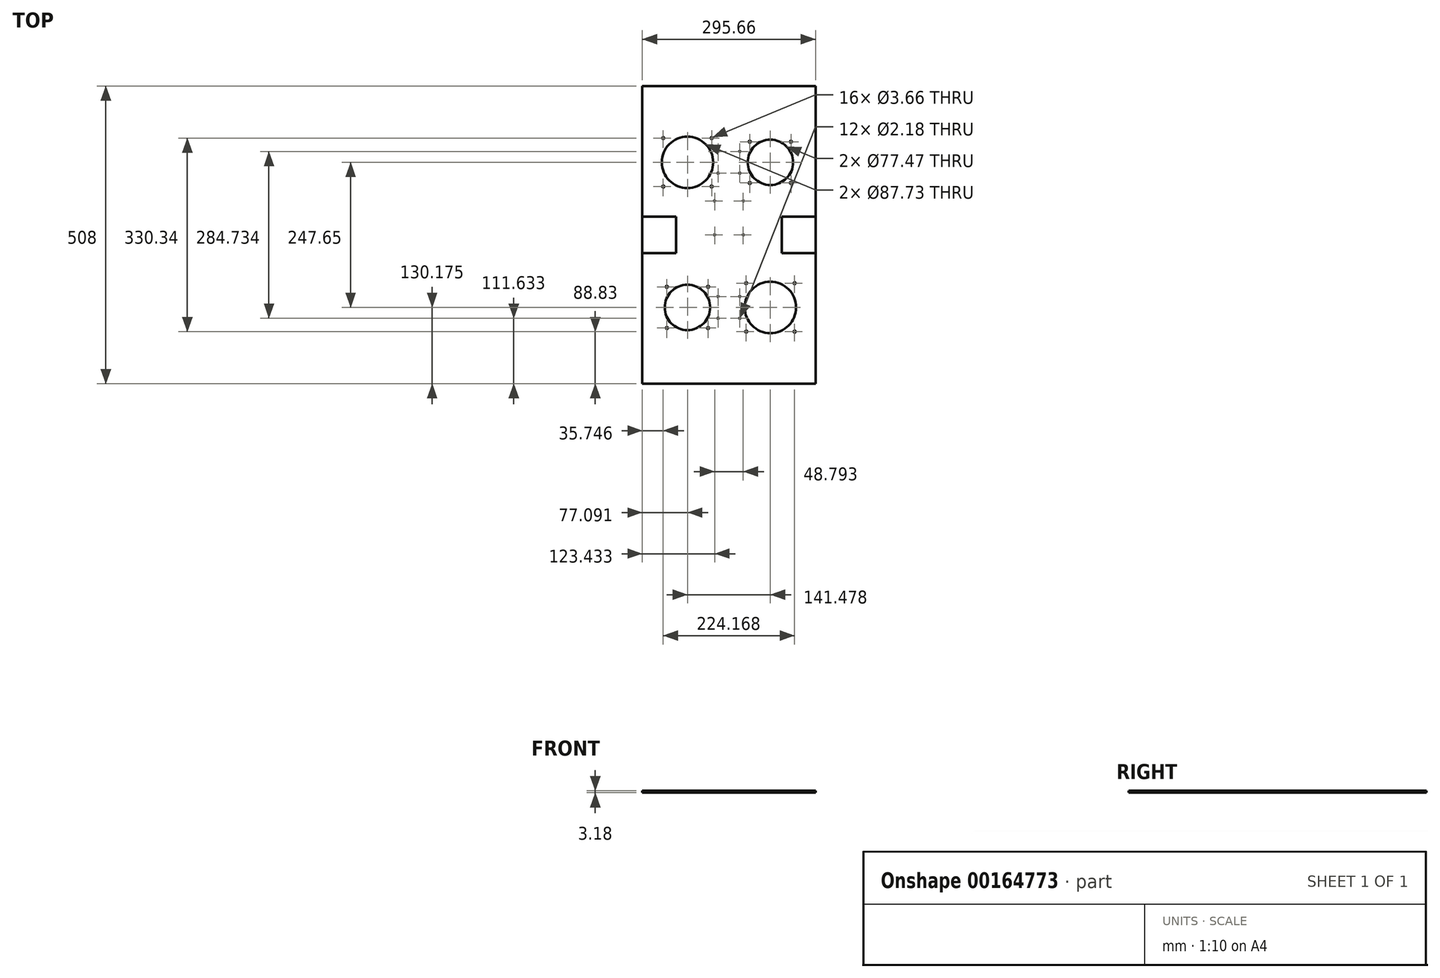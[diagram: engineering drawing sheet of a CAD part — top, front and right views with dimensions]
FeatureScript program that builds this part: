
annotation { "Feature Type Name" : "Feature", "Feature Type Description" : "" }
export const myFeature = defineFeature(function(context is Context, id is Id, definition is map)
    precondition{}
    {
        {
            var Q0;
            Q0=qCreatedBy(makeId("Top.planeOp"),FACE);
            var sketch = newSketch(context, id + "F0", { "sketchPlane" : qUnion([Q0])});
            skLineSegment(sketch, "E0.bottom", {"start": v(147.83, 254) * mm, "end": v(-147.83, 254) * mm});
            skLineSegment(sketch, "E0.top", {"start": v(147.83, -254) * mm, "end": v(-147.83, -254) * mm});
            skLineSegment(sketch, "E0.left", {"start": v(147.83, 254) * mm, "end": v(147.83, -254) * mm});
            skLineSegment(sketch, "E0.right", {"start": v(-147.83, 254) * mm, "end": v(-147.83, -254) * mm});
            skPoint(sketch, "E0.middle", {"position": v(0, 0) * mm});
            skLineSegment(sketch, "E1.bottom", {"start": v(6.35, 6.35) * mm, "end": v(-6.35, 6.35) * mm, "construction": true});
            skLineSegment(sketch, "E1.top", {"start": v(6.35, -6.35) * mm, "end": v(-6.35, -6.35) * mm, "construction": true});
            skLineSegment(sketch, "E1.left", {"start": v(6.35, 6.35) * mm, "end": v(6.35, -6.35) * mm, "construction": true});
            skLineSegment(sketch, "E1.right", {"start": v(-6.35, 6.35) * mm, "end": v(-6.35, -6.35) * mm, "construction": true});
            skLineSegment(sketch, "E2.bottom", {"start": v(6.35, 6.35) * mm, "end": v(135.13, 6.35) * mm, "construction": true});
            skLineSegment(sketch, "E2.top", {"start": v(6.35, 241.3) * mm, "end": v(135.13, 241.3) * mm, "construction": true});
            skLineSegment(sketch, "E2.left", {"start": v(6.35, 6.35) * mm, "end": v(6.35, 241.3) * mm, "construction": true});
            skLineSegment(sketch, "E2.right", {"start": v(135.13, 6.35) * mm, "end": v(135.13, 241.3) * mm, "construction": true});
            skLineSegment(sketch, "E3.bottom", {"start": v(-6.35, 6.35) * mm, "end": v(-135.13, 6.35) * mm, "construction": true});
            skLineSegment(sketch, "E3.top", {"start": v(-6.35, 241.3) * mm, "end": v(-135.13, 241.3) * mm, "construction": true});
            skLineSegment(sketch, "E3.left", {"start": v(-6.35, 6.35) * mm, "end": v(-6.35, 241.3) * mm, "construction": true});
            skLineSegment(sketch, "E3.right", {"start": v(-135.13, 6.35) * mm, "end": v(-135.13, 241.3) * mm, "construction": true});
            skLineSegment(sketch, "E4.bottom", {"start": v(-6.35, -6.35) * mm, "end": v(-135.13, -6.35) * mm, "construction": true});
            skLineSegment(sketch, "E4.top", {"start": v(-6.35, -241.3) * mm, "end": v(-135.13, -241.3) * mm, "construction": true});
            skLineSegment(sketch, "E4.left", {"start": v(-6.35, -6.35) * mm, "end": v(-6.35, -241.3) * mm, "construction": true});
            skLineSegment(sketch, "E4.right", {"start": v(-135.13, -6.35) * mm, "end": v(-135.13, -241.3) * mm, "construction": true});
            skLineSegment(sketch, "E5.bottom", {"start": v(6.35, -6.35) * mm, "end": v(135.13, -6.35) * mm, "construction": true});
            skLineSegment(sketch, "E5.top", {"start": v(6.35, -241.3) * mm, "end": v(135.13, -241.3) * mm, "construction": true});
            skLineSegment(sketch, "E5.left", {"start": v(6.35, -6.35) * mm, "end": v(6.35, -241.3) * mm, "construction": true});
            skLineSegment(sketch, "E5.right", {"start": v(135.13, -6.35) * mm, "end": v(135.13, -241.3) * mm, "construction": true});
            skLineSegment(sketch, "E6", {"start": v(-135.13, 241.3) * mm, "end": v(-147.83, 241.3) * mm, "construction": true});
            skLineSegment(sketch, "E7", {"start": v(-135.13, 241.3) * mm, "end": v(-135.13, 254) * mm, "construction": true});
            skLineSegment(sketch, "E8", {"start": v(-70.74, -6.35) * mm, "end": v(-70.74, -241.3) * mm, "construction": true});
            skLineSegment(sketch, "E9", {"start": v(70.74, -6.35) * mm, "end": v(70.74, -241.3) * mm, "construction": true});
            skLineSegment(sketch, "E10", {"start": v(-70.74, 6.35) * mm, "end": v(-70.74, 241.3) * mm, "construction": true});
            skLineSegment(sketch, "E11", {"start": v(70.74, 241.3) * mm, "end": v(70.74, 6.35) * mm, "construction": true});
            skCircle(sketch, "E12", {"center": v(-70.74, 123.82) * mm, "radius": 43.87 * mm});
            skCircle(sketch, "E13", {"center": v(70.74, 123.82) * mm, "radius": 38.73 * mm});
            skCircle(sketch, "E14", {"center": v(70.74, -123.83) * mm, "radius": 43.87 * mm});
            skCircle(sketch, "E15", {"center": v(-70.74, -123.83) * mm, "radius": 38.73 * mm});
            skLineSegment(sketch, "E16.bottom", {"start": v(-29.4, 82.48) * mm, "end": v(-112.08, 82.48) * mm, "construction": true});
            skLineSegment(sketch, "E16.top", {"start": v(-29.4, 165.17) * mm, "end": v(-112.08, 165.17) * mm, "construction": true});
            skLineSegment(sketch, "E16.left", {"start": v(-29.4, 82.48) * mm, "end": v(-29.4, 165.17) * mm, "construction": true});
            skLineSegment(sketch, "E16.right", {"start": v(-112.08, 82.48) * mm, "end": v(-112.08, 165.17) * mm, "construction": true});
            skLineSegment(sketch, "E17.bottom", {"start": v(35.59, 88.67) * mm, "end": v(105.9, 88.67) * mm, "construction": true});
            skLineSegment(sketch, "E17.top", {"start": v(35.59, 158.98) * mm, "end": v(105.9, 158.98) * mm, "construction": true});
            skLineSegment(sketch, "E17.left", {"start": v(35.59, 88.67) * mm, "end": v(35.59, 158.98) * mm, "construction": true});
            skLineSegment(sketch, "E17.right", {"start": v(105.9, 88.67) * mm, "end": v(105.9, 158.98) * mm, "construction": true});
            skLineSegment(sketch, "E18.bottom", {"start": v(112.08, -165.17) * mm, "end": v(29.4, -165.17) * mm, "construction": true});
            skLineSegment(sketch, "E18.top", {"start": v(112.08, -82.48) * mm, "end": v(29.4, -82.48) * mm, "construction": true});
            skLineSegment(sketch, "E18.left", {"start": v(112.08, -165.17) * mm, "end": v(112.08, -82.48) * mm, "construction": true});
            skLineSegment(sketch, "E18.right", {"start": v(29.4, -165.17) * mm, "end": v(29.4, -82.48) * mm, "construction": true});
            skLineSegment(sketch, "E19.bottom", {"start": v(-35.59, -158.98) * mm, "end": v(-105.9, -158.98) * mm, "construction": true});
            skLineSegment(sketch, "E19.top", {"start": v(-35.59, -88.67) * mm, "end": v(-105.9, -88.67) * mm, "construction": true});
            skLineSegment(sketch, "E19.left", {"start": v(-35.59, -158.98) * mm, "end": v(-35.59, -88.67) * mm, "construction": true});
            skLineSegment(sketch, "E19.right", {"start": v(-105.9, -158.98) * mm, "end": v(-105.9, -88.67) * mm, "construction": true});
            skCircle(sketch, "E20", {"center": v(-29.4, 165.17) * mm, "radius": 1.83 * mm});
            skCircle(sketch, "E21", {"center": v(-112.08, 165.17) * mm, "radius": 1.83 * mm});
            skCircle(sketch, "E22", {"center": v(-112.08, 82.48) * mm, "radius": 1.83 * mm});
            skCircle(sketch, "E23", {"center": v(-29.4, 82.48) * mm, "radius": 1.83 * mm});
            skCircle(sketch, "E24", {"center": v(35.59, 88.67) * mm, "radius": 1.83 * mm});
            skCircle(sketch, "E25", {"center": v(35.59, 158.98) * mm, "radius": 1.83 * mm});
            skCircle(sketch, "E26", {"center": v(105.9, 88.67) * mm, "radius": 1.83 * mm});
            skCircle(sketch, "E27", {"center": v(105.9, 158.98) * mm, "radius": 1.83 * mm});
            skCircle(sketch, "E28", {"center": v(-105.9, -88.67) * mm, "radius": 1.83 * mm});
            skCircle(sketch, "E29", {"center": v(-35.59, -88.67) * mm, "radius": 1.83 * mm});
            skCircle(sketch, "E30", {"center": v(-105.9, -158.98) * mm, "radius": 1.83 * mm});
            skCircle(sketch, "E31", {"center": v(-35.59, -158.98) * mm, "radius": 1.83 * mm});
            skCircle(sketch, "E32", {"center": v(29.4, -165.17) * mm, "radius": 1.83 * mm});
            skCircle(sketch, "E33", {"center": v(29.4, -82.48) * mm, "radius": 1.83 * mm});
            skCircle(sketch, "E34", {"center": v(112.08, -82.48) * mm, "radius": 1.83 * mm});
            skCircle(sketch, "E35", {"center": v(112.08, -165.17) * mm, "radius": 1.83 * mm});
            skSolve(sketch);
        }
        {
            var Q0;
            Q0=qSketchRegion(id+"F0",true);
            extrude(context, id + "F1", {"entities" : qUnion([Q0]), "depth" : 3.17 * mm});
        }
        {
            var Q0;
            Q0=makeQuery(id+"F1.opExtrude","CAP_FACE",FACE,{"disambiguationData":[OSD([sQuery(id+"F0.wireOp",EDGE,"E0.bottom"),sQuery(id+"F0.wireOp",EDGE,"E0.top"),sQuery(id+"F0.wireOp",EDGE,"E0.left"),sQuery(id+"F0.wireOp",EDGE,"E0.right"),sQuery(id+"F0.wireOp",EDGE,"E12"),sQuery(id+"F0.wireOp",EDGE,"E13"),sQuery(id+"F0.wireOp",EDGE,"E14"),sQuery(id+"F0.wireOp",EDGE,"E15"),sQuery(id+"F0.wireOp",EDGE,"E20"),sQuery(id+"F0.wireOp",EDGE,"E21"),sQuery(id+"F0.wireOp",EDGE,"E22"),sQuery(id+"F0.wireOp",EDGE,"E23"),sQuery(id+"F0.wireOp",EDGE,"E24"),sQuery(id+"F0.wireOp",EDGE,"E25"),sQuery(id+"F0.wireOp",EDGE,"E26"),sQuery(id+"F0.wireOp",EDGE,"E27"),sQuery(id+"F0.wireOp",EDGE,"E28"),sQuery(id+"F0.wireOp",EDGE,"E29"),sQuery(id+"F0.wireOp",EDGE,"E30"),sQuery(id+"F0.wireOp",EDGE,"E31"),sQuery(id+"F0.wireOp",EDGE,"E32"),sQuery(id+"F0.wireOp",EDGE,"E33"),sQuery(id+"F0.wireOp",EDGE,"E34"),sQuery(id+"F0.wireOp",EDGE,"E35")])],"isStart":false});
            var sketch = newSketch(context, id + "F2", { "sketchPlane" : qUnion([Q0])});
            skLineSegment(sketch, "E36.bottom", {"start": v(147.83, 31.2) * mm, "end": v(90, 31.2) * mm});
            skLineSegment(sketch, "E36.top", {"start": v(147.83, -31.2) * mm, "end": v(90, -31.2) * mm});
            skLineSegment(sketch, "E36.left", {"start": v(147.83, 31.2) * mm, "end": v(147.83, -31.2) * mm});
            skLineSegment(sketch, "E36.right", {"start": v(90, 31.2) * mm, "end": v(90, -31.2) * mm});
            skPoint(sketch, "E37", {"position": v(147.83, 0) * mm});
            skLineSegment(sketch, "E38.bottom", {"start": v(-147.83, 31.2) * mm, "end": v(-90, 31.2) * mm});
            skLineSegment(sketch, "E38.top", {"start": v(-147.83, -31.2) * mm, "end": v(-90, -31.2) * mm});
            skLineSegment(sketch, "E38.left", {"start": v(-147.83, 31.2) * mm, "end": v(-147.83, -31.2) * mm});
            skLineSegment(sketch, "E38.right", {"start": v(-90, 31.2) * mm, "end": v(-90, -31.2) * mm});
            skSolve(sketch);
        }
        {
            var Q0;
            Q0=qSketchRegion(id+"F2",true);
            extrude(context, id + "F3", {"entities" : qUnion([Q0]), "operationType" : NewBodyOperationType.ADD, "depth" : 1 / 1625.6 * mm});
        }
        {
            var Q0;
            Q0=makeQuery(id+"F1.opExtrude","CAP_FACE",FACE,{"disambiguationData":[OSD([sQuery(id+"F0.wireOp",EDGE,"E0.bottom"),sQuery(id+"F0.wireOp",EDGE,"E0.top"),sQuery(id+"F0.wireOp",EDGE,"E0.left"),sQuery(id+"F0.wireOp",EDGE,"E0.right"),sQuery(id+"F0.wireOp",EDGE,"E12"),sQuery(id+"F0.wireOp",EDGE,"E13"),sQuery(id+"F0.wireOp",EDGE,"E14"),sQuery(id+"F0.wireOp",EDGE,"E15"),sQuery(id+"F0.wireOp",EDGE,"E20"),sQuery(id+"F0.wireOp",EDGE,"E21"),sQuery(id+"F0.wireOp",EDGE,"E22"),sQuery(id+"F0.wireOp",EDGE,"E23"),sQuery(id+"F0.wireOp",EDGE,"E24"),sQuery(id+"F0.wireOp",EDGE,"E25"),sQuery(id+"F0.wireOp",EDGE,"E26"),sQuery(id+"F0.wireOp",EDGE,"E27"),sQuery(id+"F0.wireOp",EDGE,"E28"),sQuery(id+"F0.wireOp",EDGE,"E29"),sQuery(id+"F0.wireOp",EDGE,"E30"),sQuery(id+"F0.wireOp",EDGE,"E31"),sQuery(id+"F0.wireOp",EDGE,"E32"),sQuery(id+"F0.wireOp",EDGE,"E33"),sQuery(id+"F0.wireOp",EDGE,"E34"),sQuery(id+"F0.wireOp",EDGE,"E35")])],"isStart":false});
            var sketch = newSketch(context, id + "F4", { "sketchPlane" : qUnion([Q0])});
            skLineSegment(sketch, "E39", {"start": v(-70.74, 123.82) * mm, "end": v(70.74, 123.82) * mm, "construction": true});
            skLineSegment(sketch, "E40", {"start": v(-70.74, -123.83) * mm, "end": v(70.74, -123.82) * mm, "construction": true});
            skLineSegment(sketch, "E41.bottom", {"start": v(24.4, 57.86) * mm, "end": v(-24.4, 57.86) * mm, "construction": true});
            skLineSegment(sketch, "E41.top", {"start": v(24.4, 0) * mm, "end": v(-24.4, 0) * mm, "construction": true});
            skLineSegment(sketch, "E41.left", {"start": v(24.4, 57.86) * mm, "end": v(24.4, 0) * mm, "construction": true});
            skLineSegment(sketch, "E41.right", {"start": v(-24.4, 57.86) * mm, "end": v(-24.4, 0) * mm, "construction": true});
            skPoint(sketch, "E41.middle", {"position": v(0, 28.93) * mm});
            skLineSegment(sketch, "E42.bottom", {"start": v(18.54, 142.37) * mm, "end": v(-18.54, 142.37) * mm, "construction": true});
            skLineSegment(sketch, "E42.top", {"start": v(18.54, 105.28) * mm, "end": v(-18.54, 105.28) * mm, "construction": true});
            skLineSegment(sketch, "E42.left", {"start": v(18.54, 142.37) * mm, "end": v(18.54, 105.28) * mm, "construction": true});
            skLineSegment(sketch, "E42.right", {"start": v(-18.54, 142.37) * mm, "end": v(-18.54, 105.28) * mm, "construction": true});
            skPoint(sketch, "E42.middle", {"position": v(0, 123.82) * mm});
            skLineSegment(sketch, "E43.bottom", {"start": v(-18.54, -105.28) * mm, "end": v(18.54, -105.28) * mm, "construction": true});
            skLineSegment(sketch, "E43.top", {"start": v(-18.54, -142.37) * mm, "end": v(18.54, -142.37) * mm, "construction": true});
            skLineSegment(sketch, "E43.left", {"start": v(-18.54, -105.28) * mm, "end": v(-18.54, -142.37) * mm, "construction": true});
            skLineSegment(sketch, "E43.right", {"start": v(18.54, -105.28) * mm, "end": v(18.54, -142.37) * mm, "construction": true});
            skPoint(sketch, "E43.middle", {"position": v(0, -123.83) * mm});
            skCircle(sketch, "E44", {"center": v(-24.4, 0) * mm, "radius": 1.1 * mm});
            skCircle(sketch, "E45", {"center": v(24.4, 0) * mm, "radius": 1.1 * mm});
            skCircle(sketch, "E46", {"center": v(-18.54, -105.28) * mm, "radius": 1.1 * mm});
            skCircle(sketch, "E47", {"center": v(18.54, -105.28) * mm, "radius": 1.1 * mm});
            skCircle(sketch, "E48", {"center": v(18.54, -142.37) * mm, "radius": 1.1 * mm});
            skCircle(sketch, "E49", {"center": v(-18.54, -142.37) * mm, "radius": 1.1 * mm});
            skCircle(sketch, "E50", {"center": v(-18.54, 142.37) * mm, "radius": 1.1 * mm});
            skCircle(sketch, "E51", {"center": v(18.54, 142.37) * mm, "radius": 1.1 * mm});
            skCircle(sketch, "E52", {"center": v(18.54, 105.28) * mm, "radius": 1.1 * mm});
            skCircle(sketch, "E53", {"center": v(-18.54, 105.28) * mm, "radius": 1.1 * mm});
            skCircle(sketch, "E54", {"center": v(-24.4, 57.86) * mm, "radius": 1.1 * mm});
            skCircle(sketch, "E55", {"center": v(24.4, 57.86) * mm, "radius": 1.1 * mm});
            skLineSegment(sketch, "E56", {"start": v(0, 0) * mm, "end": v(0, 28.93) * mm, "construction": true});
            skLineSegment(sketch, "E57", {"start": v(-24.4, 0) * mm, "end": v(-90, 0) * mm, "construction": true});
            skSolve(sketch);
        }
        {
            var Q0;
            Q0=qSketchRegion(id+"F4",true);
            var Q1;
            Q1=makeQuery(id+"F1.opExtrude","CAP_FACE",FACE,{"disambiguationData":[OSD([sQuery(id+"F0.wireOp",EDGE,"E0.bottom"),sQuery(id+"F0.wireOp",EDGE,"E0.top"),sQuery(id+"F0.wireOp",EDGE,"E0.left"),sQuery(id+"F0.wireOp",EDGE,"E0.right"),sQuery(id+"F0.wireOp",EDGE,"E12"),sQuery(id+"F0.wireOp",EDGE,"E13"),sQuery(id+"F0.wireOp",EDGE,"E14"),sQuery(id+"F0.wireOp",EDGE,"E15"),sQuery(id+"F0.wireOp",EDGE,"E20"),sQuery(id+"F0.wireOp",EDGE,"E21"),sQuery(id+"F0.wireOp",EDGE,"E22"),sQuery(id+"F0.wireOp",EDGE,"E23"),sQuery(id+"F0.wireOp",EDGE,"E24"),sQuery(id+"F0.wireOp",EDGE,"E25"),sQuery(id+"F0.wireOp",EDGE,"E26"),sQuery(id+"F0.wireOp",EDGE,"E27"),sQuery(id+"F0.wireOp",EDGE,"E28"),sQuery(id+"F0.wireOp",EDGE,"E29"),sQuery(id+"F0.wireOp",EDGE,"E30"),sQuery(id+"F0.wireOp",EDGE,"E31"),sQuery(id+"F0.wireOp",EDGE,"E32"),sQuery(id+"F0.wireOp",EDGE,"E33"),sQuery(id+"F0.wireOp",EDGE,"E34"),sQuery(id+"F0.wireOp",EDGE,"E35")])],"isStart":true});
            extrude(context, id + "F5", {"entities" : qUnion([Q0]), "operationType" : NewBodyOperationType.REMOVE, "endBound" : BoundingType.UP_TO_SURFACE, "oppositeDirection" : true, "endBoundEntityFace" : qUnion([Q1]), "depth" : 25.4 * mm});
        }
    });
